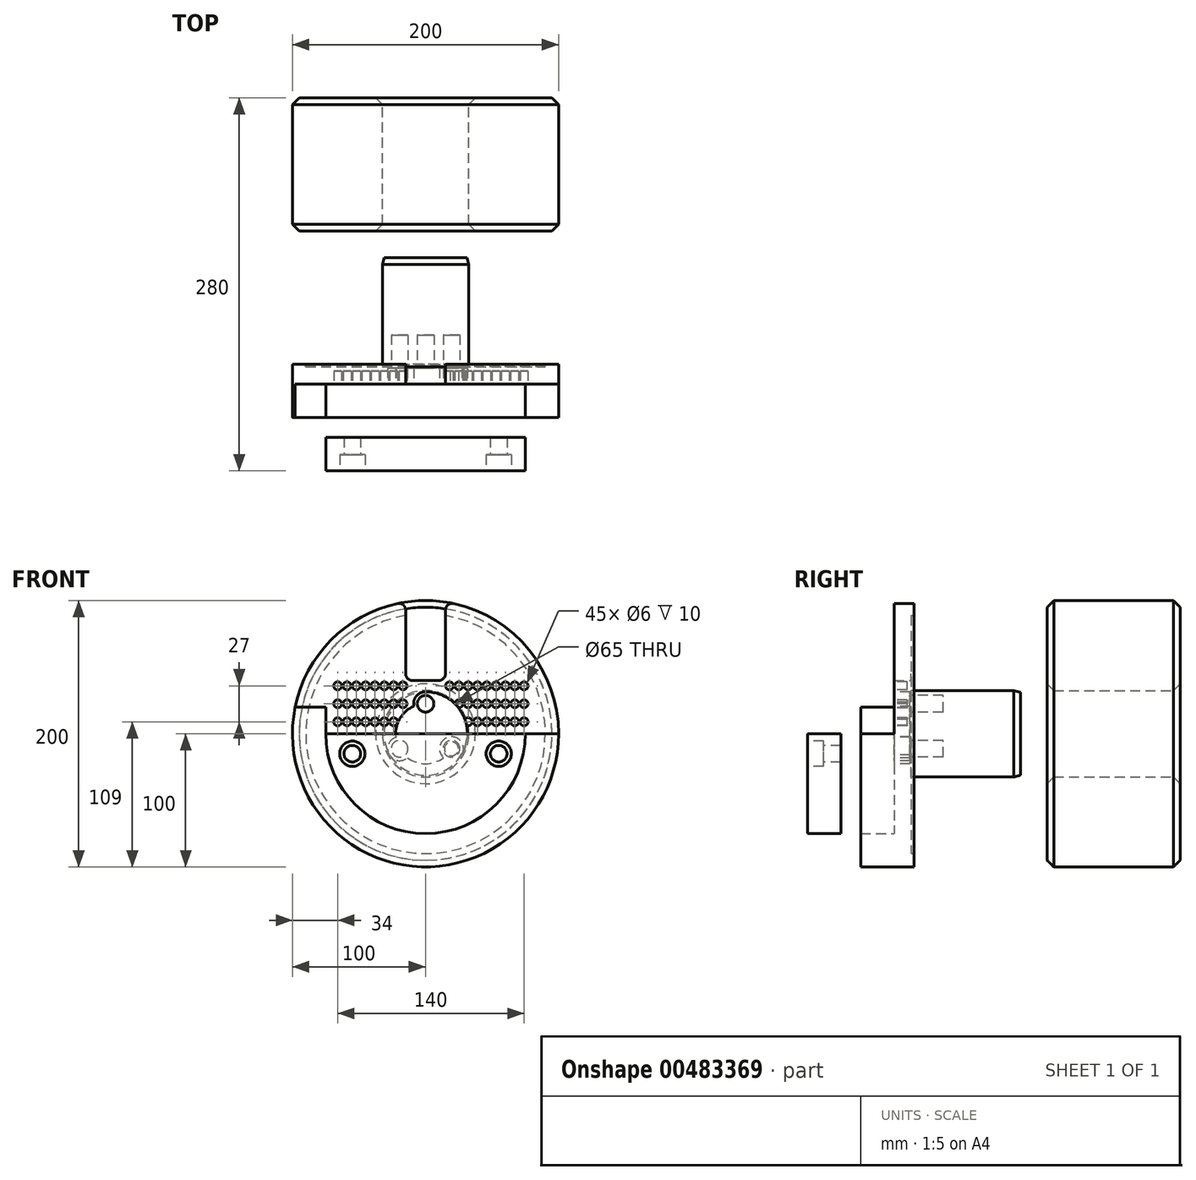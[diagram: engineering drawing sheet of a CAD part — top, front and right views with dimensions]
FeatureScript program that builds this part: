
annotation { "Feature Type Name" : "Feature", "Feature Type Description" : "" }
export const myFeature = defineFeature(function(context is Context, id is Id, definition is map)
    precondition{}
    {
        {
            var Q0;
            Q0=qCreatedBy(makeId("Front.planeOp"),FACE);
            var sketch = newSketch(context, id + "F0", { "sketchPlane" : qUnion([Q0])});
            skCircle(sketch, "E0", {"center": v(0, 0) * mm, "radius": 100 * mm});
            skCircle(sketch, "E1", {"center": v(0, 0) * mm, "radius": 32.5 * mm});
            skSolve(sketch);
        }
        {
            var Q0;
            Q0 = qSketchRegion(id + "F0", true);
            extrude(context, id + "F1", {"entities" : qUnion([Q0]), "depth" : 100 * mm});
        }
        {
            var Q0;
            Q0=makeQuery(id+"F1.opExtrude","CAP_EDGE",EDGE,{"disambiguationData":[OSD([sQuery(id+"F0.wireOp",EDGE,"E1")])],"isStart":false});
            var Q1;
            Q1=makeQuery(id+"F1.opExtrude","CAP_EDGE",EDGE,{"disambiguationData":[OSD([sQuery(id+"F0.wireOp",EDGE,"E0")])],"isStart":false});
            var Q2;
            Q2=makeQuery(id+"F1.opExtrude","CAP_EDGE",EDGE,{"disambiguationData":[OSD([sQuery(id+"F0.wireOp",EDGE,"E0")])],"isStart":true});
            var Q3;
            Q3=makeQuery(id+"F1.opExtrude","CAP_EDGE",EDGE,{"disambiguationData":[OSD([sQuery(id+"F0.wireOp",EDGE,"E1")])],"isStart":true});
            chamfer(context, id + "F2", {"entities" : qUnion([Q0, Q1, Q2, Q3]), "width" : 5 * mm, "tangentPropagation" : true});
        }
        {
            var Q0;
            Q0=makeQuery(id+"F1.opExtrude","CAP_FACE",FACE,{"disambiguationData":[OSD([sQuery(id+"F0.wireOp",EDGE,"E0"),sQuery(id+"F0.wireOp",EDGE,"E1")])],"isStart":false});
            cPlane(context, id + "F3", {"entities" : qUnion([Q0]), "cplaneType" : CPlaneType.OFFSET, "offset" : 100 * mm, "width" : 150 * mm, "height" : 150 * mm});
        }
        {
            var Q0;
            Q0=qCreatedBy(id+"F3.planeOp",FACE);
            var sketch = newSketch(context, id + "F4", { "sketchPlane" : qUnion([Q0])});
            skCircle(sketch, "E2", {"center": v(0, 0) * mm, "radius": 32.5 * mm});
            skSolve(sketch);
        }
        {
            var Q0;
            Q0 = qSketchRegion(id + "F4", true);
            extrude(context, id + "F5", {"entities" : qUnion([Q0]), "oppositeDirection" : true, "depth" : 80 * mm});
        }
        {
            var Q0;
            Q0=makeQuery(id+"F5.opExtrude","CAP_EDGE",EDGE,{"disambiguationData":[OSD([sQuery(id+"F4.wireOp",EDGE,"E2")])],"isStart":false});
            chamfer(context, id + "F6", {"entities" : qUnion([Q0]), "chamferType" : ChamferType.OFFSET_ANGLE, "width" : 5 * mm, "oppositeDirection" : false, "angle" : 15 * degree, "tangentPropagation" : true});
        }
        {
            var Q0;
            Q0=makeQuery(id+"F5.opExtrude","CAP_FACE",FACE,{"disambiguationData":[OSD([sQuery(id+"F4.wireOp",EDGE,"E2")])],"isStart":true});
            var sketch = newSketch(context, id + "F7", { "sketchPlane" : qUnion([Q0])});
            skCircle(sketch, "E3", {"center": v(0, 0) * mm, "radius": 100 * mm});
            skSolve(sketch);
        }
        {
            var Q0;
            Q0 = qSketchRegion(id + "F7", true);
            extrude(context, id + "F8", {"entities" : qUnion([Q0]), "operationType" : NewBodyOperationType.ADD, "depth" : 15 * mm});
        }
        {
            var Q0;
            Q0=makeQuery(id+"F8.opExtrude","CAP_FACE",FACE,{"disambiguationData":[OSD([sQuery(id+"F7.wireOp",EDGE,"E3")])],"isStart":true});
            var sketch = newSketch(context, id + "F9", { "sketchPlane" : qUnion([Q0])});
            skCircle(sketch, "E4", {"center": v(0, 0) * mm, "radius": 90 * mm});
            skCircle(sketch, "E5", {"center": v(0, 0) * mm, "radius": 32.5 * mm});
            skSolve(sketch);
        }
        {
            var Q0;
            Q0=makeQuery(id+"F9.imprint","IMPRINT",FACE,{"disambiguationData":[TD([[makeQuery(id+"F9.imprint","IMPRINT",EDGE,{"derivedFrom":sQuery(id+"F9.wireOp",EDGE,"E4")}),1.0]])]});
            extrude(context, id + "F10", {"entities" : qUnion([Q0]), "operationType" : NewBodyOperationType.REMOVE, "oppositeDirection" : true, "depth" : 2 * mm});
        }
        {
            var Q0;
            Q0=makeQuery(id+"F8.opExtrude","CAP_FACE",FACE,{"disambiguationData":[OSD([sQuery(id+"F7.wireOp",EDGE,"E3")])],"isStart":true});
            var sketch = newSketch(context, id + "F11", { "sketchPlane" : qUnion([Q0])});
            skLineSegment(sketch, "E6", {"start": v(0, 0) * mm, "end": v(0, 100) * mm});
            skLineSegment(sketch, "E7", {"start": v(0, 100) * mm, "end": v(15, 100) * mm});
            skLineSegment(sketch, "E8", {"start": v(15, 100) * mm, "end": v(15, 40) * mm});
            skLineSegment(sketch, "E9", {"start": v(15, 40) * mm, "end": v(-15, 40) * mm});
            skLineSegment(sketch, "E10", {"start": v(-15, 40) * mm, "end": v(-15, 100) * mm});
            skLineSegment(sketch, "E11", {"start": v(-15, 100) * mm, "end": v(0, 100) * mm});
            skSolve(sketch);
        }
        {
            var Q0;
            Q0 = qSketchRegion(id + "F11", true);
            extrude(context, id + "F12", {"entities" : qUnion([Q0]), "operationType" : NewBodyOperationType.REMOVE, "oppositeDirection" : true, "depth" : 25 * mm});
        }
        {
            var Q0;
            Q0=makeQuery(id+"F12.boolean.opBoolean","COPY",EDGE,{"derivedFrom":makeQuery(id+"F12.opExtrude","SWEPT_EDGE",EDGE,{"disambiguationData":[OSD([sQuery(id+"F11.wireOp",EDGE,"E8"),sQuery(id+"F11.wireOp",EDGE,"E9")])]})});
            var Q1;
            Q1=makeQuery(id+"F12.boolean.opBoolean","COPY",EDGE,{"derivedFrom":makeQuery(id+"F12.opExtrude","SWEPT_EDGE",EDGE,{"disambiguationData":[OSD([sQuery(id+"F11.wireOp",EDGE,"E9"),sQuery(id+"F11.wireOp",EDGE,"E10")])]})});
            var Q2;
            Q2=makeQuery(id+"F12.boolean.opBoolean","INTERSECT",EDGE,{"derivedFrom":[makeQuery(id+"F8.opExtrude","SWEPT_FACE",FACE,{"disambiguationData":[OSD([sQuery(id+"F7.wireOp",EDGE,"E3")])]}),makeQuery(id+"F12.opExtrude","SWEPT_FACE",FACE,{"disambiguationData":[OSD([sQuery(id+"F11.wireOp",EDGE,"E10")])]})]});
            var Q3;
            Q3=makeQuery(id+"F12.boolean.opBoolean","INTERSECT",EDGE,{"derivedFrom":[makeQuery(id+"F8.opExtrude","SWEPT_FACE",FACE,{"disambiguationData":[OSD([sQuery(id+"F7.wireOp",EDGE,"E3")])]}),makeQuery(id+"F12.opExtrude","SWEPT_FACE",FACE,{"disambiguationData":[OSD([sQuery(id+"F11.wireOp",EDGE,"E8")])]})]});
            fillet(context, id + "F13", {"entities" : qUnion([Q0, Q1, Q2, Q3]), "radius" : 5 * mm, "tangentPropagation" : true, "allowEdgeOverflow" : false});
        }
        {
            var Q0;
            Q0=makeQuery(id+"F8.opExtrude","CAP_FACE",FACE,{"disambiguationData":[OSD([sQuery(id+"F7.wireOp",EDGE,"E3")])],"isStart":false});
            var sketch = newSketch(context, id + "F14", { "sketchPlane" : qUnion([Q0])});
            skCircle(sketch, "E12", {"center": v(0, 0) * mm, "radius": 22.5 * mm});
            skLineSegment(sketch, "E13", {"start": v(0, 0) * mm, "end": v(0, 22.5) * mm});
            skCircle(sketch, "E14", {"center": v(0, 22.5) * mm, "radius": 9 * mm});
            skCircle(sketch, "E15", {"center": v(0, 0) * mm, "radius": 31.5 * mm});
            skCircle(sketch, "E16.1.0", {"center": v(-19.49, -11.25) * mm, "radius": 9 * mm});
            skCircle(sketch, "E16.2.0", {"center": v(19.49, -11.25) * mm, "radius": 9 * mm});
            skSolve(sketch);
        }
        {
            var Q0;
            {var subQ0=sQuery(id+"F14.wireOp",EDGE,"E13");var subQ1=sQuery(id+"F14.wireOp",EDGE,"E12");var subQ2=makeQuery(id+"F14.imprint","INTERSECT",VERTEX,{"derivedFrom":[subQ1,subQ0]});Q0=makeQuery(id+"F14.imprint","IMPRINT",FACE,{"disambiguationData":[TD([[makeQuery(id+"F14.imprint","IMPRINT",EDGE,{"disambiguationData":[TD([[subQ2,-1.0]])],"derivedFrom":subQ1}),1.0]])]});}
            var Q1;
            {var subQ0=sQuery(id+"F14.wireOp",EDGE,"E13");var subQ1=sQuery(id+"F14.wireOp",EDGE,"E12");var subQ2=makeQuery(id+"F14.imprint","INTERSECT",VERTEX,{"derivedFrom":[subQ1,subQ0]});Q1=makeQuery(id+"F14.imprint","IMPRINT",FACE,{"disambiguationData":[TD([[makeQuery(id+"F14.imprint","IMPRINT",EDGE,{"disambiguationData":[TD([[subQ2,1.0]])],"derivedFrom":subQ1}),1.0]])]});}
            var Q2;
            {var subQ0=sQuery(id+"F14.wireOp",EDGE,"E12");var subQ1=makeQuery(id+"F14.imprint","INTERSECT",VERTEX,{"derivedFrom":[subQ0,sQuery(id+"F14.wireOp",EDGE,"E13")]});Q2=makeQuery(id+"F14.imprint","IMPRINT",FACE,{"disambiguationData":[TD([[makeQuery(id+"F14.imprint","IMPRINT",EDGE,{"disambiguationData":[TD([[subQ1,1.0]])],"derivedFrom":subQ0}),-1.0]])]});}
            var Q3;
            {var subQ0=sQuery(id+"F14.wireOp",EDGE,"E16.1.0");var subQ1=sQuery(id+"F14.wireOp",EDGE,"E12");var subQ2=makeQuery(id+"F14.imprint","INTERSECT",VERTEX,{"disambiguationData":[OD(0.0)],"derivedFrom":[subQ1,subQ0]});Q3=makeQuery(id+"F14.imprint","IMPRINT",FACE,{"disambiguationData":[TD([[makeQuery(id+"F14.imprint","IMPRINT",EDGE,{"disambiguationData":[TD([[subQ2,-1.0]])],"derivedFrom":subQ1}),1.0]])]});}
            var Q4;
            {var subQ0=sQuery(id+"F14.wireOp",EDGE,"E16.1.0");var subQ1=sQuery(id+"F14.wireOp",EDGE,"E12");var subQ2=makeQuery(id+"F14.imprint","INTERSECT",VERTEX,{"disambiguationData":[OD(0.0)],"derivedFrom":[subQ1,subQ0]});Q4=makeQuery(id+"F14.imprint","IMPRINT",FACE,{"disambiguationData":[TD([[makeQuery(id+"F14.imprint","IMPRINT",EDGE,{"disambiguationData":[TD([[subQ2,-1.0]])],"derivedFrom":subQ1}),-1.0]])]});}
            var Q5;
            {var subQ0=sQuery(id+"F14.wireOp",EDGE,"E16.2.0");var subQ1=sQuery(id+"F14.wireOp",EDGE,"E12");var subQ2=makeQuery(id+"F14.imprint","INTERSECT",VERTEX,{"disambiguationData":[OD(0.0)],"derivedFrom":[subQ1,subQ0]});Q5=makeQuery(id+"F14.imprint","IMPRINT",FACE,{"disambiguationData":[TD([[makeQuery(id+"F14.imprint","IMPRINT",EDGE,{"disambiguationData":[TD([[subQ2,-1.0]])],"derivedFrom":subQ1}),-1.0]])]});}
            var Q6;
            {var subQ0=sQuery(id+"F14.wireOp",EDGE,"E16.2.0");var subQ1=sQuery(id+"F14.wireOp",EDGE,"E12");var subQ2=makeQuery(id+"F14.imprint","INTERSECT",VERTEX,{"disambiguationData":[OD(0.0)],"derivedFrom":[subQ1,subQ0]});Q6=makeQuery(id+"F14.imprint","IMPRINT",FACE,{"disambiguationData":[TD([[makeQuery(id+"F14.imprint","IMPRINT",EDGE,{"disambiguationData":[TD([[subQ2,-1.0]])],"derivedFrom":subQ1}),1.0]])]});}
            extrude(context, id + "F15", {"entities" : qUnion([Q0, Q1, Q2, Q3, Q4, Q5, Q6]), "operationType" : NewBodyOperationType.REMOVE, "oppositeDirection" : true, "depth" : 12 * mm});
        }
        {
            var Q0;
            Q0=makeQuery(id+"F15.boolean.opBoolean","COPY",FACE,{"derivedFrom":makeQuery(id+"F15.opExtrude","CAP_FACE",FACE,{"disambiguationData":[OSD([sQuery(id+"F14.wireOp",EDGE,"E14")])],"isStart":false})});
            var sketch = newSketch(context, id + "F16", { "sketchPlane" : qUnion([Q0])});
            skCircle(sketch, "E17", {"center": v(0, 22.5) * mm, "radius": 6.25 * mm});
            skCircle(sketch, "E18.1.0", {"center": v(-19.49, -11.25) * mm, "radius": 6.25 * mm});
            skCircle(sketch, "E18.2.0", {"center": v(19.49, -11.25) * mm, "radius": 6.25 * mm});
            skPoint(sketch, "E18.center", {"position": v(0, 0) * mm});
            skSolve(sketch);
        }
        {
            var Q0;
            Q0=makeQuery(id+"F16.imprint","IMPRINT",FACE,{"disambiguationData":[TD([[makeQuery(id+"F16.imprint","IMPRINT",EDGE,{"derivedFrom":sQuery(id+"F16.wireOp",EDGE,"E17")}),1.0]])]});
            var Q1;
            Q1=makeQuery(id+"F16.imprint","IMPRINT",FACE,{"disambiguationData":[TD([[makeQuery(id+"F16.imprint","IMPRINT",EDGE,{"derivedFrom":sQuery(id+"F16.wireOp",EDGE,"E18.2.0")}),1.0]])]});
            var Q2;
            Q2=makeQuery(id+"F16.imprint","IMPRINT",FACE,{"disambiguationData":[TD([[makeQuery(id+"F16.imprint","IMPRINT",EDGE,{"derivedFrom":sQuery(id+"F16.wireOp",EDGE,"E18.1.0")}),1.0]])]});
            extrude(context, id + "F17", {"entities" : qUnion([Q0, Q1, Q2]), "operationType" : NewBodyOperationType.REMOVE, "oppositeDirection" : true, "depth" : 25 * mm});
        }
        {
            var Q0;
            Q0=makeQuery(id+"F15.boolean.opBoolean","COPY",EDGE,{"derivedFrom":makeQuery(id+"F15.opExtrude","CAP_EDGE",EDGE,{"disambiguationData":[OSD([sQuery(id+"F14.wireOp",EDGE,"E14")])],"isStart":true})});
            var Q1;
            Q1=makeQuery(id+"F17.boolean.opBoolean","COPY",EDGE,{"derivedFrom":makeQuery(id+"F17.opExtrude","CAP_EDGE",EDGE,{"disambiguationData":[OSD([sQuery(id+"F16.wireOp",EDGE,"E17")])],"isStart":true})});
            var Q2;
            Q2=makeQuery(id+"F15.boolean.opBoolean","COPY",EDGE,{"derivedFrom":makeQuery(id+"F15.opExtrude","CAP_EDGE",EDGE,{"disambiguationData":[OSD([sQuery(id+"F14.wireOp",EDGE,"E16.2.0")])],"isStart":true})});
            var Q3;
            Q3=makeQuery(id+"F17.boolean.opBoolean","COPY",EDGE,{"derivedFrom":makeQuery(id+"F17.opExtrude","CAP_EDGE",EDGE,{"disambiguationData":[OSD([sQuery(id+"F16.wireOp",EDGE,"E18.2.0")])],"isStart":true})});
            var Q4;
            Q4=makeQuery(id+"F17.boolean.opBoolean","COPY",EDGE,{"derivedFrom":makeQuery(id+"F17.opExtrude","CAP_EDGE",EDGE,{"disambiguationData":[OSD([sQuery(id+"F16.wireOp",EDGE,"E18.1.0")])],"isStart":true})});
            var Q5;
            Q5=makeQuery(id+"F15.boolean.opBoolean","COPY",EDGE,{"derivedFrom":makeQuery(id+"F15.opExtrude","CAP_EDGE",EDGE,{"disambiguationData":[OSD([sQuery(id+"F14.wireOp",EDGE,"E16.1.0")])],"isStart":true})});
            chamfer(context, id + "F18", {"entities" : qUnion([Q0, Q1, Q2, Q3, Q4, Q5]), "width" : 1 * mm, "tangentPropagation" : true});
        }
        {
            var Q0;
            Q0=makeQuery(id+"F8.opExtrude","CAP_FACE",FACE,{"disambiguationData":[OSD([sQuery(id+"F7.wireOp",EDGE,"E3")])],"isStart":false});
            var sketch = newSketch(context, id + "F19", { "sketchPlane" : qUnion([Q0])});
            skArc(sketch, "E19", {"start": v(-75, 0) * mm, "mid": v(0, -75) * mm, "end": v(75, 0) * mm});
            skArc(sketch, "E20", {"start": v(-97.98, 20) * mm, "mid": v(-10.05, -99.5) * mm, "end": v(100, 0) * mm});
            skLineSegment(sketch, "E21", {"start": v(-97.98, 20) * mm, "end": v(-75, 20) * mm});
            skLineSegment(sketch, "E22", {"start": v(-75, 0) * mm, "end": v(-75, 20) * mm});
            skPoint(sketch, "E23.orphan", {"position": v(-72.28, 20) * mm});
            skLineSegment(sketch, "E24", {"start": v(-75, 0) * mm, "end": v(75, 0) * mm});
            skLineSegment(sketch, "E25", {"start": v(75, 0) * mm, "end": v(100, 0) * mm});
            skSolve(sketch);
        }
        {
            var Q0;
            Q0=makeQuery(id+"F19.imprint","IMPRINT",FACE,{"disambiguationData":[TD([[makeQuery(id+"F19.imprint","IMPRINT",EDGE,{"derivedFrom":sQuery(id+"F19.wireOp",EDGE,"E19")}),-1.0]])]});
            extrude(context, id + "F20", {"entities" : qUnion([Q0]), "operationType" : NewBodyOperationType.ADD, "depth" : 25 * mm});
        }
        {
            var Q0;
            Q0=makeQuery(id+"F8.opExtrude","CAP_FACE",FACE,{"disambiguationData":[OSD([sQuery(id+"F7.wireOp",EDGE,"E3")])],"isStart":false});
            cPlane(context, id + "F21", {"entities" : qUnion([Q0]), "cplaneType" : CPlaneType.OFFSET, "offset" : 40 * mm, "width" : 150 * mm, "height" : 150 * mm});
        }
        {
            var Q0;
            Q0=qCreatedBy(id+"F21.planeOp",FACE);
            var sketch = newSketch(context, id + "F22", { "sketchPlane" : qUnion([Q0])});
            skArc(sketch, "E26", {"start": v(-75, 0) * mm, "mid": v(0, -75) * mm, "end": v(75, 0) * mm});
            skLineSegment(sketch, "E27", {"start": v(-75, 0) * mm, "end": v(75, 0) * mm});
            skSolve(sketch);
        }
        {
            var Q0;
            Q0 = qSketchRegion(id + "F22", true);
            extrude(context, id + "F23", {"entities" : qUnion([Q0]), "depth" : 25 * mm});
        }
        {
            var Q0;
            Q0=makeQuery(id+"F23.opExtrude","CAP_FACE",FACE,{"disambiguationData":[OSD([sQuery(id+"F22.wireOp",EDGE,"E26"),sQuery(id+"F22.wireOp",EDGE,"E27")])],"isStart":false});
            var sketch = newSketch(context, id + "F24", { "sketchPlane" : qUnion([Q0])});
            skCircle(sketch, "E28", {"center": v(-55, -15) * mm, "radius": 6.25 * mm});
            skCircle(sketch, "E29", {"center": v(55, -15) * mm, "radius": 6.25 * mm});
            skCircle(sketch, "E30", {"center": v(-55, -15) * mm, "radius": 9.5 * mm});
            skCircle(sketch, "E31", {"center": v(55, -15) * mm, "radius": 9.5 * mm});
            skSolve(sketch);
        }
        {
            var Q0;
            Q0 = qSketchRegion(id + "F24", true);
            var Q1;
            Q1=makeQuery(id+"F24.imprint","IMPRINT",FACE,{"disambiguationData":[TD([[makeQuery(id+"F24.imprint","IMPRINT",EDGE,{"derivedFrom":sQuery(id+"F24.wireOp",EDGE,"E28")}),1.0]])]});
            var Q2;
            Q2=makeQuery(id+"F24.imprint","IMPRINT",FACE,{"disambiguationData":[TD([[makeQuery(id+"F24.imprint","IMPRINT",EDGE,{"derivedFrom":sQuery(id+"F24.wireOp",EDGE,"E29")}),1.0]])]});
            extrude(context, id + "F25", {"entities" : qUnion([Q0, Q1, Q2]), "operationType" : NewBodyOperationType.REMOVE, "oppositeDirection" : true, "depth" : 12 * mm});
        }
        {
            var Q0;
            Q0=makeQuery(id+"F25.boolean.opBoolean","COPY",FACE,{"derivedFrom":makeQuery(id+"F25.opExtrude","CAP_FACE",FACE,{"disambiguationData":[OSD([sQuery(id+"F24.wireOp",EDGE,"E30")])],"isStart":false})});
            var sketch = newSketch(context, id + "F26", { "sketchPlane" : qUnion([Q0])});
            skCircle(sketch, "E32", {"center": v(-55, -15) * mm, "radius": 6.25 * mm});
            skCircle(sketch, "E33", {"center": v(55, -15) * mm, "radius": 6.25 * mm});
            skSolve(sketch);
        }
        {
            var Q0;
            Q0 = qSketchRegion(id + "F26", true);
            extrude(context, id + "F27", {"entities" : qUnion([Q0]), "operationType" : NewBodyOperationType.REMOVE, "oppositeDirection" : true, "depth" : 15 * mm});
        }
        {
            var Q0;
            Q0=makeQuery(id+"F8.opExtrude","CAP_FACE",FACE,{"disambiguationData":[OSD([sQuery(id+"F7.wireOp",EDGE,"E3")])],"isStart":false});
            var sketch = newSketch(context, id + "F28", { "sketchPlane" : qUnion([Q0])});
            skCircle(sketch, "E34", {"center": v(-66, 9) * mm, "radius": 3 * mm});
            skCircle(sketch, "E35.1.0.0", {"center": v(-59, 9) * mm, "radius": 3 * mm});
            skCircle(sketch, "E35.2.0.0", {"center": v(-52, 9) * mm, "radius": 3 * mm});
            skCircle(sketch, "E35.3.0.0", {"center": v(-45, 9) * mm, "radius": 3 * mm});
            skCircle(sketch, "E35.4.0.0", {"center": v(-38, 9) * mm, "radius": 3 * mm});
            skCircle(sketch, "E35.5.0.0", {"center": v(-31, 9) * mm, "radius": 3 * mm});
            skCircle(sketch, "E35.6.0.0", {"center": v(-24, 9) * mm, "radius": 3 * mm});
            skCircle(sketch, "E35.7.0.0", {"center": v(-17, 9) * mm, "radius": 3 * mm});
            skCircle(sketch, "E35.8.0.0", {"center": v(-10, 9) * mm, "radius": 3 * mm});
            skCircle(sketch, "E35.9.0.0", {"center": v(-3, 9) * mm, "radius": 3 * mm});
            skCircle(sketch, "E35.10.0.0", {"center": v(4, 9) * mm, "radius": 3 * mm});
            skCircle(sketch, "E35.11.0.0", {"center": v(11, 9) * mm, "radius": 3 * mm});
            skCircle(sketch, "E35.12.0.0", {"center": v(18, 9) * mm, "radius": 3 * mm});
            skCircle(sketch, "E35.13.0.0", {"center": v(25, 9) * mm, "radius": 3 * mm});
            skCircle(sketch, "E35.14.0.0", {"center": v(32, 9) * mm, "radius": 3 * mm});
            skCircle(sketch, "E35.15.0.0", {"center": v(39, 9) * mm, "radius": 3 * mm});
            skCircle(sketch, "E35.16.0.0", {"center": v(46, 9) * mm, "radius": 3 * mm});
            skCircle(sketch, "E35.17.0.0", {"center": v(53, 9) * mm, "radius": 3 * mm});
            skCircle(sketch, "E35.18.0.0", {"center": v(60, 9) * mm, "radius": 3 * mm});
            skCircle(sketch, "E35.19.0.0", {"center": v(67, 9) * mm, "radius": 3 * mm});
            skCircle(sketch, "E35.20.0.0", {"center": v(74, 9) * mm, "radius": 3 * mm});
            skLineSegment(sketch, "E35.direction1", {"start": v(-66, 9) * mm, "end": v(-59, 9) * mm, "construction": true});
            skCircle(sketch, "E36.0.1.0", {"center": v(-66, 36) * mm, "radius": 3 * mm});
            skCircle(sketch, "E36.0.1.1", {"center": v(-59, 36) * mm, "radius": 3 * mm});
            skCircle(sketch, "E36.0.1.2", {"center": v(-52, 36) * mm, "radius": 3 * mm});
            skCircle(sketch, "E36.0.1.3", {"center": v(-45, 36) * mm, "radius": 3 * mm});
            skCircle(sketch, "E36.0.1.4", {"center": v(-38, 36) * mm, "radius": 3 * mm});
            skCircle(sketch, "E36.0.1.5", {"center": v(-31, 36) * mm, "radius": 3 * mm});
            skCircle(sketch, "E36.0.1.6", {"center": v(-24, 36) * mm, "radius": 3 * mm});
            skCircle(sketch, "E36.0.1.7", {"center": v(-17, 36) * mm, "radius": 3 * mm});
            skCircle(sketch, "E36.0.1.8", {"center": v(-10, 36) * mm, "radius": 3 * mm});
            skCircle(sketch, "E36.0.1.9", {"center": v(-3, 36) * mm, "radius": 3 * mm});
            skCircle(sketch, "E36.0.1.10", {"center": v(4, 36) * mm, "radius": 3 * mm});
            skCircle(sketch, "E36.0.1.11", {"center": v(11, 36) * mm, "radius": 3 * mm});
            skCircle(sketch, "E36.0.1.12", {"center": v(18, 36) * mm, "radius": 3 * mm});
            skCircle(sketch, "E36.0.1.13", {"center": v(25, 36) * mm, "radius": 3 * mm});
            skCircle(sketch, "E36.0.1.14", {"center": v(32, 36) * mm, "radius": 3 * mm});
            skCircle(sketch, "E36.0.1.15", {"center": v(39, 36) * mm, "radius": 3 * mm});
            skCircle(sketch, "E36.0.1.16", {"center": v(46, 36) * mm, "radius": 3 * mm});
            skCircle(sketch, "E36.0.1.17", {"center": v(53, 36) * mm, "radius": 3 * mm});
            skCircle(sketch, "E36.0.1.18", {"center": v(60, 36) * mm, "radius": 3 * mm});
            skCircle(sketch, "E36.0.1.19", {"center": v(67, 36) * mm, "radius": 3 * mm});
            skCircle(sketch, "E36.0.1.20", {"center": v(74, 36) * mm, "radius": 3 * mm});
            skLineSegment(sketch, "E36.direction1", {"start": v(-65, 8) * mm, "end": v(-40, 8) * mm, "construction": true});
            skLineSegment(sketch, "E36.direction2", {"start": v(-65, 8) * mm, "end": v(-65, 36.32) * mm, "construction": true});
            skCircle(sketch, "E37.0.1.0", {"center": v(-66, 22.5) * mm, "radius": 3 * mm});
            skCircle(sketch, "E37.0.1.1", {"center": v(-59, 22.5) * mm, "radius": 3 * mm});
            skCircle(sketch, "E37.0.1.2", {"center": v(-52, 22.5) * mm, "radius": 3 * mm});
            skCircle(sketch, "E37.0.1.3", {"center": v(-45, 22.5) * mm, "radius": 3 * mm});
            skCircle(sketch, "E37.0.1.4", {"center": v(-38, 22.5) * mm, "radius": 3 * mm});
            skCircle(sketch, "E37.0.1.5", {"center": v(-31, 22.5) * mm, "radius": 3 * mm});
            skCircle(sketch, "E37.0.1.6", {"center": v(-24, 22.5) * mm, "radius": 3 * mm});
            skCircle(sketch, "E37.0.1.7", {"center": v(-17, 22.5) * mm, "radius": 3 * mm});
            skCircle(sketch, "E37.0.1.8", {"center": v(18, 22.5) * mm, "radius": 3 * mm});
            skCircle(sketch, "E37.0.1.9", {"center": v(25, 22.5) * mm, "radius": 3 * mm});
            skCircle(sketch, "E37.0.1.10", {"center": v(32, 22.5) * mm, "radius": 3 * mm});
            skCircle(sketch, "E37.0.1.11", {"center": v(39, 22.5) * mm, "radius": 3 * mm});
            skCircle(sketch, "E37.0.1.12", {"center": v(46, 22.5) * mm, "radius": 3 * mm});
            skCircle(sketch, "E37.0.1.13", {"center": v(53, 22.5) * mm, "radius": 3 * mm});
            skCircle(sketch, "E37.0.1.14", {"center": v(60, 22.5) * mm, "radius": 3 * mm});
            skCircle(sketch, "E37.0.1.15", {"center": v(67, 22.5) * mm, "radius": 3 * mm});
            skCircle(sketch, "E37.0.1.16", {"center": v(74, 22.5) * mm, "radius": 3 * mm});
            skLineSegment(sketch, "E37.direction1", {"start": v(-66, 9) * mm, "end": v(-40, 9) * mm, "construction": true});
            skLineSegment(sketch, "E37.direction2", {"start": v(-66, 9) * mm, "end": v(-66, 22.5) * mm, "construction": true});
            skSolve(sketch);
        }
        {
            var Q0;
            {var subQ0=sQuery(id+"F28.wireOp",EDGE,"E35.1.0.0");var subQ1=sQuery(id+"F28.wireOp",EDGE,"lmhidIYx-T9QX-L1YV-YhIe-0UZypUjT4fYJ");var subQ2=makeQuery(id+"F28.imprint","INTERSECT",VERTEX,{"disambiguationData":[OD(0.0)],"derivedFrom":[subQ1,subQ0]});Q0=makeQuery(id+"F28.imprint","IMPRINT",FACE,{"disambiguationData":[TD([[makeQuery(id+"F28.imprint","IMPRINT",EDGE,{"disambiguationData":[TD([[subQ2,-1.0]])],"derivedFrom":subQ1}),-1.0]])]});}
            var Q1;
            {var subQ0=sQuery(id+"F28.wireOp",EDGE,"E35.2.0.0");var subQ1=sQuery(id+"F28.wireOp",EDGE,"lmhidIYx-T9QX-L1YV-YhIe-0UZypUjT4fYJ");var subQ2=makeQuery(id+"F28.imprint","INTERSECT",VERTEX,{"disambiguationData":[OD(0.0)],"derivedFrom":[subQ1,subQ0]});Q1=makeQuery(id+"F28.imprint","IMPRINT",FACE,{"disambiguationData":[TD([[makeQuery(id+"F28.imprint","IMPRINT",EDGE,{"disambiguationData":[TD([[subQ2,-1.0]])],"derivedFrom":subQ1}),-1.0]])]});}
            var Q2;
            {var subQ0=sQuery(id+"F28.wireOp",EDGE,"E35.2.0.0");var subQ1=sQuery(id+"F28.wireOp",EDGE,"lmhidIYx-T9QX-L1YV-YhIe-0UZypUjT4fYJ");var subQ2=makeQuery(id+"F28.imprint","INTERSECT",VERTEX,{"disambiguationData":[OD(0.0)],"derivedFrom":[subQ1,subQ0]});Q2=makeQuery(id+"F28.imprint","IMPRINT",FACE,{"disambiguationData":[TD([[makeQuery(id+"F28.imprint","IMPRINT",EDGE,{"disambiguationData":[TD([[subQ2,-1.0]])],"derivedFrom":subQ1}),1.0]])]});}
            var Q3;
            {var subQ0=sQuery(id+"F28.wireOp",EDGE,"E35.3.0.0");var subQ1=sQuery(id+"F28.wireOp",EDGE,"lmhidIYx-T9QX-L1YV-YhIe-0UZypUjT4fYJ");var subQ2=makeQuery(id+"F28.imprint","INTERSECT",VERTEX,{"disambiguationData":[OD(0.0)],"derivedFrom":[subQ1,subQ0]});Q3=makeQuery(id+"F28.imprint","IMPRINT",FACE,{"disambiguationData":[TD([[makeQuery(id+"F28.imprint","IMPRINT",EDGE,{"disambiguationData":[TD([[subQ2,-1.0]])],"derivedFrom":subQ1}),-1.0]])]});}
            var Q4;
            {var subQ0=sQuery(id+"F28.wireOp",EDGE,"E35.4.0.0");var subQ1=sQuery(id+"F28.wireOp",EDGE,"lmhidIYx-T9QX-L1YV-YhIe-0UZypUjT4fYJ");var subQ2=makeQuery(id+"F28.imprint","INTERSECT",VERTEX,{"disambiguationData":[OD(0.0)],"derivedFrom":[subQ1,subQ0]});Q4=makeQuery(id+"F28.imprint","IMPRINT",FACE,{"disambiguationData":[TD([[makeQuery(id+"F28.imprint","IMPRINT",EDGE,{"disambiguationData":[TD([[subQ2,-1.0]])],"derivedFrom":subQ1}),1.0]])]});}
            var Q5;
            {var subQ0=sQuery(id+"F28.wireOp",EDGE,"E35.5.0.0");var subQ1=sQuery(id+"F28.wireOp",EDGE,"lmhidIYx-T9QX-L1YV-YhIe-0UZypUjT4fYJ");var subQ2=makeQuery(id+"F28.imprint","INTERSECT",VERTEX,{"disambiguationData":[OD(0.0)],"derivedFrom":[subQ1,subQ0]});Q5=makeQuery(id+"F28.imprint","IMPRINT",FACE,{"disambiguationData":[TD([[makeQuery(id+"F28.imprint","IMPRINT",EDGE,{"disambiguationData":[TD([[subQ2,-1.0]])],"derivedFrom":subQ1}),1.0]])]});}
            var Q6;
            {var subQ0=sQuery(id+"F28.wireOp",EDGE,"E35.6.0.0");var subQ1=sQuery(id+"F28.wireOp",EDGE,"lmhidIYx-T9QX-L1YV-YhIe-0UZypUjT4fYJ");var subQ2=makeQuery(id+"F28.imprint","INTERSECT",VERTEX,{"disambiguationData":[OD(0.0)],"derivedFrom":[subQ1,subQ0]});Q6=makeQuery(id+"F28.imprint","IMPRINT",FACE,{"disambiguationData":[TD([[makeQuery(id+"F28.imprint","IMPRINT",EDGE,{"disambiguationData":[TD([[subQ2,-1.0]])],"derivedFrom":subQ1}),1.0]])]});}
            var Q7;
            {var subQ0=sQuery(id+"F28.wireOp",EDGE,"E35.8.0.0");var subQ1=sQuery(id+"F28.wireOp",EDGE,"lmhidIYx-T9QX-L1YV-YhIe-0UZypUjT4fYJ");var subQ2=makeQuery(id+"F28.imprint","INTERSECT",VERTEX,{"disambiguationData":[OD(0.0)],"derivedFrom":[subQ1,subQ0]});Q7=makeQuery(id+"F28.imprint","IMPRINT",FACE,{"disambiguationData":[TD([[makeQuery(id+"F28.imprint","IMPRINT",EDGE,{"disambiguationData":[TD([[subQ2,-1.0]])],"derivedFrom":subQ1}),1.0]])]});}
            var Q8;
            {var subQ0=sQuery(id+"F28.wireOp",EDGE,"E35.9.0.0");var subQ1=sQuery(id+"F28.wireOp",EDGE,"lmhidIYx-T9QX-L1YV-YhIe-0UZypUjT4fYJ");var subQ2=makeQuery(id+"F28.imprint","INTERSECT",VERTEX,{"disambiguationData":[OD(0.0)],"derivedFrom":[subQ1,subQ0]});Q8=makeQuery(id+"F28.imprint","IMPRINT",FACE,{"disambiguationData":[TD([[makeQuery(id+"F28.imprint","IMPRINT",EDGE,{"disambiguationData":[TD([[subQ2,1.0]])],"derivedFrom":subQ1}),-1.0]])]});}
            var Q9;
            {var subQ0=sQuery(id+"F28.wireOp",EDGE,"E35.9.0.0");var subQ1=sQuery(id+"F28.wireOp",EDGE,"lmhidIYx-T9QX-L1YV-YhIe-0UZypUjT4fYJ");var subQ2=makeQuery(id+"F28.imprint","INTERSECT",VERTEX,{"disambiguationData":[OD(0.0)],"derivedFrom":[subQ1,subQ0]});Q9=makeQuery(id+"F28.imprint","IMPRINT",FACE,{"disambiguationData":[TD([[makeQuery(id+"F28.imprint","IMPRINT",EDGE,{"disambiguationData":[TD([[subQ2,1.0]])],"derivedFrom":subQ1}),1.0]])]});}
            var Q10;
            {var subQ0=sQuery(id+"F28.wireOp",EDGE,"E35.10.0.0");var subQ1=sQuery(id+"F28.wireOp",EDGE,"lmhidIYx-T9QX-L1YV-YhIe-0UZypUjT4fYJ");var subQ2=makeQuery(id+"F28.imprint","INTERSECT",VERTEX,{"disambiguationData":[OD(0.0)],"derivedFrom":[subQ1,subQ0]});Q10=makeQuery(id+"F28.imprint","IMPRINT",FACE,{"disambiguationData":[TD([[makeQuery(id+"F28.imprint","IMPRINT",EDGE,{"disambiguationData":[TD([[subQ2,-1.0]])],"derivedFrom":subQ1}),1.0]])]});}
            var Q11;
            {var subQ0=sQuery(id+"F28.wireOp",EDGE,"E35.11.0.0");var subQ1=sQuery(id+"F28.wireOp",EDGE,"lmhidIYx-T9QX-L1YV-YhIe-0UZypUjT4fYJ");var subQ2=makeQuery(id+"F28.imprint","INTERSECT",VERTEX,{"disambiguationData":[OD(0.0)],"derivedFrom":[subQ1,subQ0]});Q11=makeQuery(id+"F28.imprint","IMPRINT",FACE,{"disambiguationData":[TD([[makeQuery(id+"F28.imprint","IMPRINT",EDGE,{"disambiguationData":[TD([[subQ2,-1.0]])],"derivedFrom":subQ1}),-1.0]])]});}
            var Q12;
            {var subQ0=sQuery(id+"F28.wireOp",EDGE,"E35.12.0.0");var subQ1=sQuery(id+"F28.wireOp",EDGE,"lmhidIYx-T9QX-L1YV-YhIe-0UZypUjT4fYJ");var subQ2=makeQuery(id+"F28.imprint","INTERSECT",VERTEX,{"disambiguationData":[OD(0.0)],"derivedFrom":[subQ1,subQ0]});Q12=makeQuery(id+"F28.imprint","IMPRINT",FACE,{"disambiguationData":[TD([[makeQuery(id+"F28.imprint","IMPRINT",EDGE,{"disambiguationData":[TD([[subQ2,-1.0]])],"derivedFrom":subQ1}),1.0]])]});}
            var Q13;
            {var subQ0=sQuery(id+"F28.wireOp",EDGE,"E35.13.0.0");var subQ1=sQuery(id+"F28.wireOp",EDGE,"lmhidIYx-T9QX-L1YV-YhIe-0UZypUjT4fYJ");var subQ2=makeQuery(id+"F28.imprint","INTERSECT",VERTEX,{"disambiguationData":[OD(0.0)],"derivedFrom":[subQ1,subQ0]});Q13=makeQuery(id+"F28.imprint","IMPRINT",FACE,{"disambiguationData":[TD([[makeQuery(id+"F28.imprint","IMPRINT",EDGE,{"disambiguationData":[TD([[subQ2,-1.0]])],"derivedFrom":subQ1}),-1.0]])]});}
            var Q14;
            {var subQ0=sQuery(id+"F28.wireOp",EDGE,"E35.13.0.0");var subQ1=sQuery(id+"F28.wireOp",EDGE,"lmhidIYx-T9QX-L1YV-YhIe-0UZypUjT4fYJ");var subQ2=makeQuery(id+"F28.imprint","INTERSECT",VERTEX,{"disambiguationData":[OD(0.0)],"derivedFrom":[subQ1,subQ0]});Q14=makeQuery(id+"F28.imprint","IMPRINT",FACE,{"disambiguationData":[TD([[makeQuery(id+"F28.imprint","IMPRINT",EDGE,{"disambiguationData":[TD([[subQ2,-1.0]])],"derivedFrom":subQ1}),1.0]])]});}
            var Q15;
            {var subQ0=sQuery(id+"F28.wireOp",EDGE,"E35.14.0.0");var subQ1=sQuery(id+"F28.wireOp",EDGE,"lmhidIYx-T9QX-L1YV-YhIe-0UZypUjT4fYJ");var subQ2=makeQuery(id+"F28.imprint","INTERSECT",VERTEX,{"disambiguationData":[OD(0.0)],"derivedFrom":[subQ1,subQ0]});Q15=makeQuery(id+"F28.imprint","IMPRINT",FACE,{"disambiguationData":[TD([[makeQuery(id+"F28.imprint","IMPRINT",EDGE,{"disambiguationData":[TD([[subQ2,-1.0]])],"derivedFrom":subQ1}),-1.0]])]});}
            var Q16;
            {var subQ0=sQuery(id+"F28.wireOp",EDGE,"E35.15.0.0");var subQ1=sQuery(id+"F28.wireOp",EDGE,"lmhidIYx-T9QX-L1YV-YhIe-0UZypUjT4fYJ");var subQ2=makeQuery(id+"F28.imprint","INTERSECT",VERTEX,{"disambiguationData":[OD(0.0)],"derivedFrom":[subQ1,subQ0]});Q16=makeQuery(id+"F28.imprint","IMPRINT",FACE,{"disambiguationData":[TD([[makeQuery(id+"F28.imprint","IMPRINT",EDGE,{"disambiguationData":[TD([[subQ2,-1.0]])],"derivedFrom":subQ1}),-1.0]])]});}
            var Q17;
            {var subQ0=sQuery(id+"F28.wireOp",EDGE,"E35.16.0.0");var subQ1=sQuery(id+"F28.wireOp",EDGE,"lmhidIYx-T9QX-L1YV-YhIe-0UZypUjT4fYJ");var subQ2=makeQuery(id+"F28.imprint","INTERSECT",VERTEX,{"disambiguationData":[OD(0.0)],"derivedFrom":[subQ1,subQ0]});Q17=makeQuery(id+"F28.imprint","IMPRINT",FACE,{"disambiguationData":[TD([[makeQuery(id+"F28.imprint","IMPRINT",EDGE,{"disambiguationData":[TD([[subQ2,-1.0]])],"derivedFrom":subQ1}),1.0]])]});}
            var Q18;
            {var subQ0=sQuery(id+"F28.wireOp",EDGE,"E35.16.0.0");var subQ1=sQuery(id+"F28.wireOp",EDGE,"lmhidIYx-T9QX-L1YV-YhIe-0UZypUjT4fYJ");var subQ2=makeQuery(id+"F28.imprint","INTERSECT",VERTEX,{"disambiguationData":[OD(0.0)],"derivedFrom":[subQ1,subQ0]});Q18=makeQuery(id+"F28.imprint","IMPRINT",FACE,{"disambiguationData":[TD([[makeQuery(id+"F28.imprint","IMPRINT",EDGE,{"disambiguationData":[TD([[subQ2,-1.0]])],"derivedFrom":subQ1}),-1.0]])]});}
            var Q19;
            {var subQ0=sQuery(id+"F28.wireOp",EDGE,"E35.17.0.0");var subQ1=sQuery(id+"F28.wireOp",EDGE,"lmhidIYx-T9QX-L1YV-YhIe-0UZypUjT4fYJ");var subQ2=makeQuery(id+"F28.imprint","INTERSECT",VERTEX,{"disambiguationData":[OD(0.0)],"derivedFrom":[subQ1,subQ0]});Q19=makeQuery(id+"F28.imprint","IMPRINT",FACE,{"disambiguationData":[TD([[makeQuery(id+"F28.imprint","IMPRINT",EDGE,{"disambiguationData":[TD([[subQ2,-1.0]])],"derivedFrom":subQ1}),-1.0]])]});}
            var Q20;
            {var subQ0=sQuery(id+"F28.wireOp",EDGE,"E35.17.0.0");var subQ1=sQuery(id+"F28.wireOp",EDGE,"lmhidIYx-T9QX-L1YV-YhIe-0UZypUjT4fYJ");var subQ2=makeQuery(id+"F28.imprint","INTERSECT",VERTEX,{"disambiguationData":[OD(0.0)],"derivedFrom":[subQ1,subQ0]});Q20=makeQuery(id+"F28.imprint","IMPRINT",FACE,{"disambiguationData":[TD([[makeQuery(id+"F28.imprint","IMPRINT",EDGE,{"disambiguationData":[TD([[subQ2,-1.0]])],"derivedFrom":subQ1}),1.0]])]});}
            var Q21;
            {var subQ0=sQuery(id+"F28.wireOp",EDGE,"E35.18.0.0");var subQ1=sQuery(id+"F28.wireOp",EDGE,"lmhidIYx-T9QX-L1YV-YhIe-0UZypUjT4fYJ");var subQ2=makeQuery(id+"F28.imprint","INTERSECT",VERTEX,{"disambiguationData":[OD(0.0)],"derivedFrom":[subQ1,subQ0]});Q21=makeQuery(id+"F28.imprint","IMPRINT",FACE,{"disambiguationData":[TD([[makeQuery(id+"F28.imprint","IMPRINT",EDGE,{"disambiguationData":[TD([[subQ2,-1.0]])],"derivedFrom":subQ1}),1.0]])]});}
            var Q22;
            {var subQ0=sQuery(id+"F28.wireOp",EDGE,"E35.18.0.0");var subQ1=sQuery(id+"F28.wireOp",EDGE,"lmhidIYx-T9QX-L1YV-YhIe-0UZypUjT4fYJ");var subQ2=makeQuery(id+"F28.imprint","INTERSECT",VERTEX,{"disambiguationData":[OD(0.0)],"derivedFrom":[subQ1,subQ0]});Q22=makeQuery(id+"F28.imprint","IMPRINT",FACE,{"disambiguationData":[TD([[makeQuery(id+"F28.imprint","IMPRINT",EDGE,{"disambiguationData":[TD([[subQ2,-1.0]])],"derivedFrom":subQ1}),-1.0]])]});}
            var Q23;
            Q23=makeQuery(id+"F28.imprint","IMPRINT",FACE,{"disambiguationData":[TD([[makeQuery(id+"F28.imprint","IMPRINT",EDGE,{"derivedFrom":sQuery(id+"F28.wireOp",EDGE,"E35.20.0.0")}),1.0]])]});
            var Q24;
            {var subQ0=sQuery(id+"F28.wireOp",EDGE,"E35.1.0.0");var subQ1=sQuery(id+"F28.wireOp",EDGE,"lmhidIYx-T9QX-L1YV-YhIe-0UZypUjT4fYJ");var subQ2=makeQuery(id+"F28.imprint","INTERSECT",VERTEX,{"disambiguationData":[OD(0.0)],"derivedFrom":[subQ1,subQ0]});Q24=makeQuery(id+"F28.imprint","IMPRINT",FACE,{"disambiguationData":[TD([[makeQuery(id+"F28.imprint","IMPRINT",EDGE,{"disambiguationData":[TD([[subQ2,-1.0]])],"derivedFrom":subQ1}),1.0]])]});}
            var Q25;
            {var subQ0=sQuery(id+"F28.wireOp",EDGE,"E35.3.0.0");var subQ1=sQuery(id+"F28.wireOp",EDGE,"lmhidIYx-T9QX-L1YV-YhIe-0UZypUjT4fYJ");var subQ2=makeQuery(id+"F28.imprint","INTERSECT",VERTEX,{"disambiguationData":[OD(0.0)],"derivedFrom":[subQ1,subQ0]});Q25=makeQuery(id+"F28.imprint","IMPRINT",FACE,{"disambiguationData":[TD([[makeQuery(id+"F28.imprint","IMPRINT",EDGE,{"disambiguationData":[TD([[subQ2,-1.0]])],"derivedFrom":subQ1}),1.0]])]});}
            var Q26;
            {var subQ0=sQuery(id+"F28.wireOp",EDGE,"E35.4.0.0");var subQ1=sQuery(id+"F28.wireOp",EDGE,"lmhidIYx-T9QX-L1YV-YhIe-0UZypUjT4fYJ");var subQ2=makeQuery(id+"F28.imprint","INTERSECT",VERTEX,{"disambiguationData":[OD(0.0)],"derivedFrom":[subQ1,subQ0]});Q26=makeQuery(id+"F28.imprint","IMPRINT",FACE,{"disambiguationData":[TD([[makeQuery(id+"F28.imprint","IMPRINT",EDGE,{"disambiguationData":[TD([[subQ2,-1.0]])],"derivedFrom":subQ1}),-1.0]])]});}
            var Q27;
            {var subQ0=sQuery(id+"F28.wireOp",EDGE,"E35.5.0.0");var subQ1=sQuery(id+"F28.wireOp",EDGE,"lmhidIYx-T9QX-L1YV-YhIe-0UZypUjT4fYJ");var subQ2=makeQuery(id+"F28.imprint","INTERSECT",VERTEX,{"disambiguationData":[OD(0.0)],"derivedFrom":[subQ1,subQ0]});Q27=makeQuery(id+"F28.imprint","IMPRINT",FACE,{"disambiguationData":[TD([[makeQuery(id+"F28.imprint","IMPRINT",EDGE,{"disambiguationData":[TD([[subQ2,-1.0]])],"derivedFrom":subQ1}),-1.0]])]});}
            var Q28;
            {var subQ0=sQuery(id+"F28.wireOp",EDGE,"E35.6.0.0");var subQ1=sQuery(id+"F28.wireOp",EDGE,"lmhidIYx-T9QX-L1YV-YhIe-0UZypUjT4fYJ");var subQ2=makeQuery(id+"F28.imprint","INTERSECT",VERTEX,{"disambiguationData":[OD(0.0)],"derivedFrom":[subQ1,subQ0]});Q28=makeQuery(id+"F28.imprint","IMPRINT",FACE,{"disambiguationData":[TD([[makeQuery(id+"F28.imprint","IMPRINT",EDGE,{"disambiguationData":[TD([[subQ2,-1.0]])],"derivedFrom":subQ1}),-1.0]])]});}
            var Q29;
            {var subQ0=sQuery(id+"F28.wireOp",EDGE,"E35.7.0.0");var subQ1=sQuery(id+"F28.wireOp",EDGE,"lmhidIYx-T9QX-L1YV-YhIe-0UZypUjT4fYJ");var subQ2=makeQuery(id+"F28.imprint","INTERSECT",VERTEX,{"disambiguationData":[OD(0.0)],"derivedFrom":[subQ1,subQ0]});Q29=makeQuery(id+"F28.imprint","IMPRINT",FACE,{"disambiguationData":[TD([[makeQuery(id+"F28.imprint","IMPRINT",EDGE,{"disambiguationData":[TD([[subQ2,-1.0]])],"derivedFrom":subQ1}),-1.0]])]});}
            var Q30;
            {var subQ0=sQuery(id+"F28.wireOp",EDGE,"E35.7.0.0");var subQ1=sQuery(id+"F28.wireOp",EDGE,"lmhidIYx-T9QX-L1YV-YhIe-0UZypUjT4fYJ");var subQ2=makeQuery(id+"F28.imprint","INTERSECT",VERTEX,{"disambiguationData":[OD(0.0)],"derivedFrom":[subQ1,subQ0]});Q30=makeQuery(id+"F28.imprint","IMPRINT",FACE,{"disambiguationData":[TD([[makeQuery(id+"F28.imprint","IMPRINT",EDGE,{"disambiguationData":[TD([[subQ2,-1.0]])],"derivedFrom":subQ1}),1.0]])]});}
            var Q31;
            {var subQ0=sQuery(id+"F28.wireOp",EDGE,"E35.8.0.0");var subQ1=sQuery(id+"F28.wireOp",EDGE,"lmhidIYx-T9QX-L1YV-YhIe-0UZypUjT4fYJ");var subQ2=makeQuery(id+"F28.imprint","INTERSECT",VERTEX,{"disambiguationData":[OD(0.0)],"derivedFrom":[subQ1,subQ0]});Q31=makeQuery(id+"F28.imprint","IMPRINT",FACE,{"disambiguationData":[TD([[makeQuery(id+"F28.imprint","IMPRINT",EDGE,{"disambiguationData":[TD([[subQ2,-1.0]])],"derivedFrom":subQ1}),-1.0]])]});}
            var Q32;
            {var subQ0=sQuery(id+"F28.wireOp",EDGE,"E35.10.0.0");var subQ1=sQuery(id+"F28.wireOp",EDGE,"lmhidIYx-T9QX-L1YV-YhIe-0UZypUjT4fYJ");var subQ2=makeQuery(id+"F28.imprint","INTERSECT",VERTEX,{"disambiguationData":[OD(0.0)],"derivedFrom":[subQ1,subQ0]});Q32=makeQuery(id+"F28.imprint","IMPRINT",FACE,{"disambiguationData":[TD([[makeQuery(id+"F28.imprint","IMPRINT",EDGE,{"disambiguationData":[TD([[subQ2,-1.0]])],"derivedFrom":subQ1}),-1.0]])]});}
            var Q33;
            {var subQ0=sQuery(id+"F28.wireOp",EDGE,"E35.12.0.0");var subQ1=sQuery(id+"F28.wireOp",EDGE,"lmhidIYx-T9QX-L1YV-YhIe-0UZypUjT4fYJ");var subQ2=makeQuery(id+"F28.imprint","INTERSECT",VERTEX,{"disambiguationData":[OD(0.0)],"derivedFrom":[subQ1,subQ0]});Q33=makeQuery(id+"F28.imprint","IMPRINT",FACE,{"disambiguationData":[TD([[makeQuery(id+"F28.imprint","IMPRINT",EDGE,{"disambiguationData":[TD([[subQ2,-1.0]])],"derivedFrom":subQ1}),-1.0]])]});}
            var Q34;
            {var subQ0=sQuery(id+"F28.wireOp",EDGE,"E35.15.0.0");var subQ1=sQuery(id+"F28.wireOp",EDGE,"lmhidIYx-T9QX-L1YV-YhIe-0UZypUjT4fYJ");var subQ2=makeQuery(id+"F28.imprint","INTERSECT",VERTEX,{"disambiguationData":[OD(0.0)],"derivedFrom":[subQ1,subQ0]});Q34=makeQuery(id+"F28.imprint","IMPRINT",FACE,{"disambiguationData":[TD([[makeQuery(id+"F28.imprint","IMPRINT",EDGE,{"disambiguationData":[TD([[subQ2,-1.0]])],"derivedFrom":subQ1}),1.0]])]});}
            var Q35;
            Q35=makeQuery(id+"F28.imprint","IMPRINT",FACE,{"disambiguationData":[TD([[makeQuery(id+"F28.imprint","IMPRINT",EDGE,{"derivedFrom":sQuery(id+"F28.wireOp",EDGE,"E35.19.0.0")}),1.0]])]});
            var Q36;
            Q36=makeQuery(id+"F28.imprint","IMPRINT",FACE,{"disambiguationData":[TD([[makeQuery(id+"F28.imprint","IMPRINT",EDGE,{"derivedFrom":sQuery(id+"F28.wireOp",EDGE,"E35.19.0.0")}),1.0]])]});
            var Q37;
            {var subQ0=sQuery(id+"F28.wireOp",EDGE,"E35.11.0.0");var subQ1=sQuery(id+"F28.wireOp",EDGE,"lmhidIYx-T9QX-L1YV-YhIe-0UZypUjT4fYJ");var subQ2=makeQuery(id+"F28.imprint","INTERSECT",VERTEX,{"disambiguationData":[OD(0.0)],"derivedFrom":[subQ1,subQ0]});Q37=makeQuery(id+"F28.imprint","IMPRINT",FACE,{"disambiguationData":[TD([[makeQuery(id+"F28.imprint","IMPRINT",EDGE,{"disambiguationData":[TD([[subQ2,-1.0]])],"derivedFrom":subQ1}),1.0]])]});}
            var Q38;
            {var subQ0=sQuery(id+"F28.wireOp",EDGE,"E34");var subQ1=sQuery(id+"F28.wireOp",EDGE,"lmhidIYx-T9QX-L1YV-YhIe-0UZypUjT4fYJ");var subQ2=makeQuery(id+"F28.imprint","INTERSECT",VERTEX,{"disambiguationData":[OD(0.0)],"derivedFrom":[subQ1,subQ0]});Q38=makeQuery(id+"F28.imprint","IMPRINT",FACE,{"disambiguationData":[TD([[makeQuery(id+"F28.imprint","IMPRINT",EDGE,{"disambiguationData":[TD([[subQ2,-1.0]])],"derivedFrom":subQ1}),-1.0]])]});}
            var Q39;
            {var subQ0=sQuery(id+"F28.wireOp",EDGE,"E34");var subQ1=sQuery(id+"F28.wireOp",EDGE,"lmhidIYx-T9QX-L1YV-YhIe-0UZypUjT4fYJ");var subQ2=makeQuery(id+"F28.imprint","INTERSECT",VERTEX,{"disambiguationData":[OD(0.0)],"derivedFrom":[subQ1,subQ0]});Q39=makeQuery(id+"F28.imprint","IMPRINT",FACE,{"disambiguationData":[TD([[makeQuery(id+"F28.imprint","IMPRINT",EDGE,{"disambiguationData":[TD([[subQ2,-1.0]])],"derivedFrom":subQ1}),1.0]])]});}
            var Q40;
            {var subQ0=sQuery(id+"F28.wireOp",EDGE,"E35.14.0.0");var subQ1=sQuery(id+"F28.wireOp",EDGE,"lmhidIYx-T9QX-L1YV-YhIe-0UZypUjT4fYJ");var subQ2=makeQuery(id+"F28.imprint","INTERSECT",VERTEX,{"disambiguationData":[OD(0.0)],"derivedFrom":[subQ1,subQ0]});Q40=makeQuery(id+"F28.imprint","IMPRINT",FACE,{"disambiguationData":[TD([[makeQuery(id+"F28.imprint","IMPRINT",EDGE,{"disambiguationData":[TD([[subQ2,-1.0]])],"derivedFrom":subQ1}),1.0]])]});}
            var Q41;
            {var subQ0=sQuery(id+"F28.wireOp",EDGE,"E35.9.0.0");var subQ1=makeQuery(id+"F18.opChamfer","BLEND_EDGE",EDGE,{"blendedFrom":[makeQuery(id+"F15.boolean.opBoolean","COPY",EDGE,{"derivedFrom":makeQuery(id+"F15.opExtrude","CAP_EDGE",EDGE,{"disambiguationData":[OSD([sQuery(id+"F14.wireOp",EDGE,"E14")])],"isStart":true})}),makeQuery(id+"F8.opExtrude","CAP_FACE",FACE,{"disambiguationData":[OSD([sQuery(id+"F7.wireOp",EDGE,"E3")])],"isStart":false})],"blendedInto":[makeQuery(id+"F8.opExtrude","CAP_FACE",FACE,{"disambiguationData":[OSD([sQuery(id+"F7.wireOp",EDGE,"E3")])],"isStart":false})]});var subQ2=makeQuery(id+"F28.imprint","INTERSECT",VERTEX,{"disambiguationData":[OD(0.0)],"derivedFrom":[subQ1,subQ0]});Q41=makeQuery(id+"F28.imprint","IMPRINT",FACE,{"disambiguationData":[TD([[makeQuery(id+"F28.imprint","IMPRINT",EDGE,{"disambiguationData":[TD([[subQ2,-1.0]])],"derivedFrom":subQ0}),1.0]])]});}
            var Q42;
            Q42=makeQuery(id+"F28.imprint","IMPRINT",FACE,{"disambiguationData":[TD([[makeQuery(id+"F28.imprint","IMPRINT",EDGE,{"derivedFrom":sQuery(id+"F28.wireOp",EDGE,"E35.18.0.0")}),1.0]])]});
            var Q43;
            Q43=makeQuery(id+"F28.imprint","IMPRINT",FACE,{"disambiguationData":[TD([[makeQuery(id+"F28.imprint","IMPRINT",EDGE,{"derivedFrom":sQuery(id+"F28.wireOp",EDGE,"E35.17.0.0")}),1.0]])]});
            var Q44;
            Q44=makeQuery(id+"F28.imprint","IMPRINT",FACE,{"disambiguationData":[TD([[makeQuery(id+"F28.imprint","IMPRINT",EDGE,{"derivedFrom":sQuery(id+"F28.wireOp",EDGE,"E35.16.0.0")}),1.0]])]});
            var Q45;
            Q45=makeQuery(id+"F28.imprint","IMPRINT",FACE,{"disambiguationData":[TD([[makeQuery(id+"F28.imprint","IMPRINT",EDGE,{"derivedFrom":sQuery(id+"F28.wireOp",EDGE,"E35.15.0.0")}),1.0]])]});
            var Q46;
            Q46=makeQuery(id+"F28.imprint","IMPRINT",FACE,{"disambiguationData":[TD([[makeQuery(id+"F28.imprint","IMPRINT",EDGE,{"derivedFrom":sQuery(id+"F28.wireOp",EDGE,"E35.14.0.0")}),1.0]])]});
            var Q47;
            Q47=makeQuery(id+"F28.imprint","IMPRINT",FACE,{"disambiguationData":[TD([[makeQuery(id+"F28.imprint","IMPRINT",EDGE,{"derivedFrom":sQuery(id+"F28.wireOp",EDGE,"E35.13.0.0")}),1.0]])]});
            var Q48;
            Q48=makeQuery(id+"F28.imprint","IMPRINT",FACE,{"disambiguationData":[TD([[makeQuery(id+"F28.imprint","IMPRINT",EDGE,{"derivedFrom":sQuery(id+"F28.wireOp",EDGE,"E35.12.0.0")}),1.0]])]});
            var Q49;
            Q49=makeQuery(id+"F28.imprint","IMPRINT",FACE,{"disambiguationData":[TD([[makeQuery(id+"F28.imprint","IMPRINT",EDGE,{"derivedFrom":sQuery(id+"F28.wireOp",EDGE,"E35.7.0.0")}),1.0]])]});
            var Q50;
            Q50=makeQuery(id+"F28.imprint","IMPRINT",FACE,{"disambiguationData":[TD([[makeQuery(id+"F28.imprint","IMPRINT",EDGE,{"derivedFrom":sQuery(id+"F28.wireOp",EDGE,"E35.6.0.0")}),1.0]])]});
            var Q51;
            Q51=makeQuery(id+"F28.imprint","IMPRINT",FACE,{"disambiguationData":[TD([[makeQuery(id+"F28.imprint","IMPRINT",EDGE,{"derivedFrom":sQuery(id+"F28.wireOp",EDGE,"E35.5.0.0")}),1.0]])]});
            var Q52;
            Q52=makeQuery(id+"F28.imprint","IMPRINT",FACE,{"disambiguationData":[TD([[makeQuery(id+"F28.imprint","IMPRINT",EDGE,{"derivedFrom":sQuery(id+"F28.wireOp",EDGE,"E35.4.0.0")}),1.0]])]});
            var Q53;
            Q53=makeQuery(id+"F28.imprint","IMPRINT",FACE,{"disambiguationData":[TD([[makeQuery(id+"F28.imprint","IMPRINT",EDGE,{"derivedFrom":sQuery(id+"F28.wireOp",EDGE,"E36.0.1.20")}),1.0]])]});
            var Q54;
            Q54=makeQuery(id+"F28.imprint","IMPRINT",FACE,{"disambiguationData":[TD([[makeQuery(id+"F28.imprint","IMPRINT",EDGE,{"derivedFrom":sQuery(id+"F28.wireOp",EDGE,"E36.0.1.19")}),1.0]])]});
            var Q55;
            Q55=makeQuery(id+"F28.imprint","IMPRINT",FACE,{"disambiguationData":[TD([[makeQuery(id+"F28.imprint","IMPRINT",EDGE,{"derivedFrom":sQuery(id+"F28.wireOp",EDGE,"E36.0.1.18")}),1.0]])]});
            var Q56;
            Q56=makeQuery(id+"F28.imprint","IMPRINT",FACE,{"disambiguationData":[TD([[makeQuery(id+"F28.imprint","IMPRINT",EDGE,{"derivedFrom":sQuery(id+"F28.wireOp",EDGE,"E36.0.1.17")}),1.0]])]});
            var Q57;
            Q57=makeQuery(id+"F28.imprint","IMPRINT",FACE,{"disambiguationData":[TD([[makeQuery(id+"F28.imprint","IMPRINT",EDGE,{"derivedFrom":sQuery(id+"F28.wireOp",EDGE,"E36.0.1.15")}),1.0]])]});
            var Q58;
            Q58=makeQuery(id+"F28.imprint","IMPRINT",FACE,{"disambiguationData":[TD([[makeQuery(id+"F28.imprint","IMPRINT",EDGE,{"derivedFrom":sQuery(id+"F28.wireOp",EDGE,"E36.0.1.14")}),1.0]])]});
            var Q59;
            Q59=makeQuery(id+"F28.imprint","IMPRINT",FACE,{"disambiguationData":[TD([[makeQuery(id+"F28.imprint","IMPRINT",EDGE,{"derivedFrom":sQuery(id+"F28.wireOp",EDGE,"E36.0.1.13")}),1.0]])]});
            var Q60;
            Q60=makeQuery(id+"F28.imprint","IMPRINT",FACE,{"disambiguationData":[TD([[makeQuery(id+"F28.imprint","IMPRINT",EDGE,{"derivedFrom":sQuery(id+"F28.wireOp",EDGE,"E36.0.1.7")}),1.0]])]});
            var Q61;
            Q61=makeQuery(id+"F28.imprint","IMPRINT",FACE,{"disambiguationData":[TD([[makeQuery(id+"F28.imprint","IMPRINT",EDGE,{"derivedFrom":sQuery(id+"F28.wireOp",EDGE,"E35.3.0.0")}),1.0]])]});
            var Q62;
            Q62=makeQuery(id+"F28.imprint","IMPRINT",FACE,{"disambiguationData":[TD([[makeQuery(id+"F28.imprint","IMPRINT",EDGE,{"derivedFrom":sQuery(id+"F28.wireOp",EDGE,"E35.2.0.0")}),1.0]])]});
            var Q63;
            Q63=makeQuery(id+"F28.imprint","IMPRINT",FACE,{"disambiguationData":[TD([[makeQuery(id+"F28.imprint","IMPRINT",EDGE,{"derivedFrom":sQuery(id+"F28.wireOp",EDGE,"E36.0.1.1")}),1.0]])]});
            var Q64;
            Q64=makeQuery(id+"F28.imprint","IMPRINT",FACE,{"disambiguationData":[TD([[makeQuery(id+"F28.imprint","IMPRINT",EDGE,{"derivedFrom":sQuery(id+"F28.wireOp",EDGE,"E36.0.1.4")}),1.0]])]});
            var Q65;
            Q65=makeQuery(id+"F28.imprint","IMPRINT",FACE,{"disambiguationData":[TD([[makeQuery(id+"F28.imprint","IMPRINT",EDGE,{"derivedFrom":sQuery(id+"F28.wireOp",EDGE,"E36.0.1.5")}),1.0]])]});
            var Q66;
            Q66=makeQuery(id+"F28.imprint","IMPRINT",FACE,{"disambiguationData":[TD([[makeQuery(id+"F28.imprint","IMPRINT",EDGE,{"derivedFrom":sQuery(id+"F28.wireOp",EDGE,"E36.0.1.16")}),1.0]])]});
            var Q67;
            Q67=makeQuery(id+"F28.imprint","IMPRINT",FACE,{"disambiguationData":[TD([[makeQuery(id+"F28.imprint","IMPRINT",EDGE,{"derivedFrom":sQuery(id+"F28.wireOp",EDGE,"E36.0.1.12")}),1.0]])]});
            var Q68;
            Q68=makeQuery(id+"F28.imprint","IMPRINT",FACE,{"disambiguationData":[TD([[makeQuery(id+"F28.imprint","IMPRINT",EDGE,{"derivedFrom":sQuery(id+"F28.wireOp",EDGE,"E36.0.1.6")}),1.0]])]});
            var Q69;
            Q69=makeQuery(id+"F28.imprint","IMPRINT",FACE,{"disambiguationData":[TD([[makeQuery(id+"F28.imprint","IMPRINT",EDGE,{"derivedFrom":sQuery(id+"F28.wireOp",EDGE,"E36.0.1.2")}),1.0]])]});
            var Q70;
            Q70=makeQuery(id+"F28.imprint","IMPRINT",FACE,{"disambiguationData":[TD([[makeQuery(id+"F28.imprint","IMPRINT",EDGE,{"derivedFrom":sQuery(id+"F28.wireOp",EDGE,"E36.0.1.0")}),1.0]])]});
            var Q71;
            Q71=makeQuery(id+"F28.imprint","IMPRINT",FACE,{"disambiguationData":[TD([[makeQuery(id+"F28.imprint","IMPRINT",EDGE,{"derivedFrom":sQuery(id+"F28.wireOp",EDGE,"E36.0.1.3")}),1.0]])]});
            var Q72;
            Q72=makeQuery(id+"F28.imprint","IMPRINT",FACE,{"disambiguationData":[TD([[makeQuery(id+"F28.imprint","IMPRINT",EDGE,{"derivedFrom":sQuery(id+"F28.wireOp",EDGE,"E35.1.0.0")}),1.0]])]});
            var Q73;
            Q73=makeQuery(id+"F28.imprint","IMPRINT",FACE,{"disambiguationData":[TD([[makeQuery(id+"F28.imprint","IMPRINT",EDGE,{"derivedFrom":sQuery(id+"F28.wireOp",EDGE,"E34")}),1.0]])]});
            var Q74;
            Q74=makeQuery(id+"F28.imprint","IMPRINT",FACE,{"disambiguationData":[TD([[makeQuery(id+"F28.imprint","IMPRINT",EDGE,{"derivedFrom":sQuery(id+"F28.wireOp",EDGE,"E37.0.1.2")}),1.0]])]});
            var Q75;
            Q75=makeQuery(id+"F28.imprint","IMPRINT",FACE,{"disambiguationData":[TD([[makeQuery(id+"F28.imprint","IMPRINT",EDGE,{"derivedFrom":sQuery(id+"F28.wireOp",EDGE,"E37.0.1.3")}),1.0]])]});
            var Q76;
            Q76=makeQuery(id+"F28.imprint","IMPRINT",FACE,{"disambiguationData":[TD([[makeQuery(id+"F28.imprint","IMPRINT",EDGE,{"derivedFrom":sQuery(id+"F28.wireOp",EDGE,"E37.0.1.4")}),1.0]])]});
            var Q77;
            Q77=makeQuery(id+"F28.imprint","IMPRINT",FACE,{"disambiguationData":[TD([[makeQuery(id+"F28.imprint","IMPRINT",EDGE,{"derivedFrom":sQuery(id+"F28.wireOp",EDGE,"E37.0.1.5")}),1.0]])]});
            var Q78;
            Q78=makeQuery(id+"F28.imprint","IMPRINT",FACE,{"disambiguationData":[TD([[makeQuery(id+"F28.imprint","IMPRINT",EDGE,{"derivedFrom":sQuery(id+"F28.wireOp",EDGE,"E37.0.1.6")}),1.0]])]});
            var Q79;
            Q79=makeQuery(id+"F28.imprint","IMPRINT",FACE,{"disambiguationData":[TD([[makeQuery(id+"F28.imprint","IMPRINT",EDGE,{"derivedFrom":sQuery(id+"F28.wireOp",EDGE,"E37.0.1.7")}),1.0]])]});
            var Q80;
            Q80=makeQuery(id+"F28.imprint","IMPRINT",FACE,{"disambiguationData":[TD([[makeQuery(id+"F28.imprint","IMPRINT",EDGE,{"derivedFrom":sQuery(id+"F28.wireOp",EDGE,"E37.0.1.8")}),1.0]])]});
            var Q81;
            Q81=makeQuery(id+"F28.imprint","IMPRINT",FACE,{"disambiguationData":[TD([[makeQuery(id+"F28.imprint","IMPRINT",EDGE,{"derivedFrom":sQuery(id+"F28.wireOp",EDGE,"E37.0.1.9")}),1.0]])]});
            var Q82;
            Q82=makeQuery(id+"F28.imprint","IMPRINT",FACE,{"disambiguationData":[TD([[makeQuery(id+"F28.imprint","IMPRINT",EDGE,{"derivedFrom":sQuery(id+"F28.wireOp",EDGE,"E37.0.1.10")}),1.0]])]});
            var Q83;
            Q83=makeQuery(id+"F28.imprint","IMPRINT",FACE,{"disambiguationData":[TD([[makeQuery(id+"F28.imprint","IMPRINT",EDGE,{"derivedFrom":sQuery(id+"F28.wireOp",EDGE,"E37.0.1.11")}),1.0]])]});
            var Q84;
            Q84=makeQuery(id+"F28.imprint","IMPRINT",FACE,{"disambiguationData":[TD([[makeQuery(id+"F28.imprint","IMPRINT",EDGE,{"derivedFrom":sQuery(id+"F28.wireOp",EDGE,"E37.0.1.12")}),1.0]])]});
            var Q85;
            Q85=makeQuery(id+"F28.imprint","IMPRINT",FACE,{"disambiguationData":[TD([[makeQuery(id+"F28.imprint","IMPRINT",EDGE,{"derivedFrom":sQuery(id+"F28.wireOp",EDGE,"E37.0.1.13")}),1.0]])]});
            var Q86;
            Q86=makeQuery(id+"F28.imprint","IMPRINT",FACE,{"disambiguationData":[TD([[makeQuery(id+"F28.imprint","IMPRINT",EDGE,{"derivedFrom":sQuery(id+"F28.wireOp",EDGE,"E37.0.1.14")}),1.0]])]});
            var Q87;
            Q87=makeQuery(id+"F28.imprint","IMPRINT",FACE,{"disambiguationData":[TD([[makeQuery(id+"F28.imprint","IMPRINT",EDGE,{"derivedFrom":sQuery(id+"F28.wireOp",EDGE,"E37.0.1.15")}),1.0]])]});
            var Q88;
            Q88=makeQuery(id+"F28.imprint","IMPRINT",FACE,{"disambiguationData":[TD([[makeQuery(id+"F28.imprint","IMPRINT",EDGE,{"derivedFrom":sQuery(id+"F28.wireOp",EDGE,"E37.0.1.16")}),1.0]])]});
            var Q89;
            Q89=makeQuery(id+"F28.imprint","IMPRINT",FACE,{"disambiguationData":[TD([[makeQuery(id+"F28.imprint","IMPRINT",EDGE,{"derivedFrom":sQuery(id+"F28.wireOp",EDGE,"E37.0.1.1")}),1.0]])]});
            var Q90;
            Q90=makeQuery(id+"F28.imprint","IMPRINT",FACE,{"disambiguationData":[TD([[makeQuery(id+"F28.imprint","IMPRINT",EDGE,{"derivedFrom":sQuery(id+"F28.wireOp",EDGE,"E37.0.1.0")}),1.0]])]});
            extrude(context, id + "F29", {"entities" : qUnion([Q0, Q1, Q2, Q3, Q4, Q5, Q6, Q7, Q8, Q9, Q10, Q11, Q12, Q13, Q14, Q15, Q16, Q17, Q18, Q19, Q20, Q21, Q22, Q23, Q24, Q25, Q26, Q27, Q28, Q29, Q30, Q31, Q32, Q33, Q34, Q35, Q36, Q37, Q38, Q39, Q40, Q41, Q42, Q43, Q44, Q45, Q46, Q47, Q48, Q49, Q50, Q51, Q52, Q53, Q54, Q55, Q56, Q57, Q58, Q59, Q60, Q61, Q62, Q63, Q64, Q65, Q66, Q67, Q68, Q69, Q70, Q71, Q72, Q73, Q74, Q75, Q76, Q77, Q78, Q79, Q80, Q81, Q82, Q83, Q84, Q85, Q86, Q87, Q88, Q89, Q90]), "operationType" : NewBodyOperationType.REMOVE, "oppositeDirection" : true, "depth" : 10 * mm});
        }
    });
